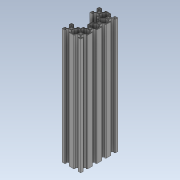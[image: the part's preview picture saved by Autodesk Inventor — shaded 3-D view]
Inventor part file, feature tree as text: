
AUTODESK INVENTOR PART (.ipt)
format: ipt  version: 2022 (Build 260153000, 153)  size: 450,048 bytes
history: native  units: mm
features: extrude x1, sketch x1
ambient origin geometry x8: Origin, YZ Plane, XZ Plane, XY Plane, X Axis, Y Axis, Z Axis, Center Point
bodies: Solid1 (feature_tree)
feature tree (2):
  extrude  "Extrusion1"  Depth=1.8mm
  sketch  "Sketch1"  dims[d2=6.5mm d3=1.8mm d4=0.5mm d5=45.0deg d7=1.8mm d8=2.0mm d9=2.0mm d12=4.6mm d13=7.7mm d14=7.7mm d15=1.8mm d16=1.8mm d17=45.0deg d18=45.0deg d19=4.05mm d20=1.35mm d21=2.0mm d22=0.5mm d24=1.8mm d25=1.35mm d26=1.35mm d27=1.35mm d28=3.15mm d29=2.0mm d30=135.0deg d31=3.15mm d32=250.0mm d33=0.0mm]
